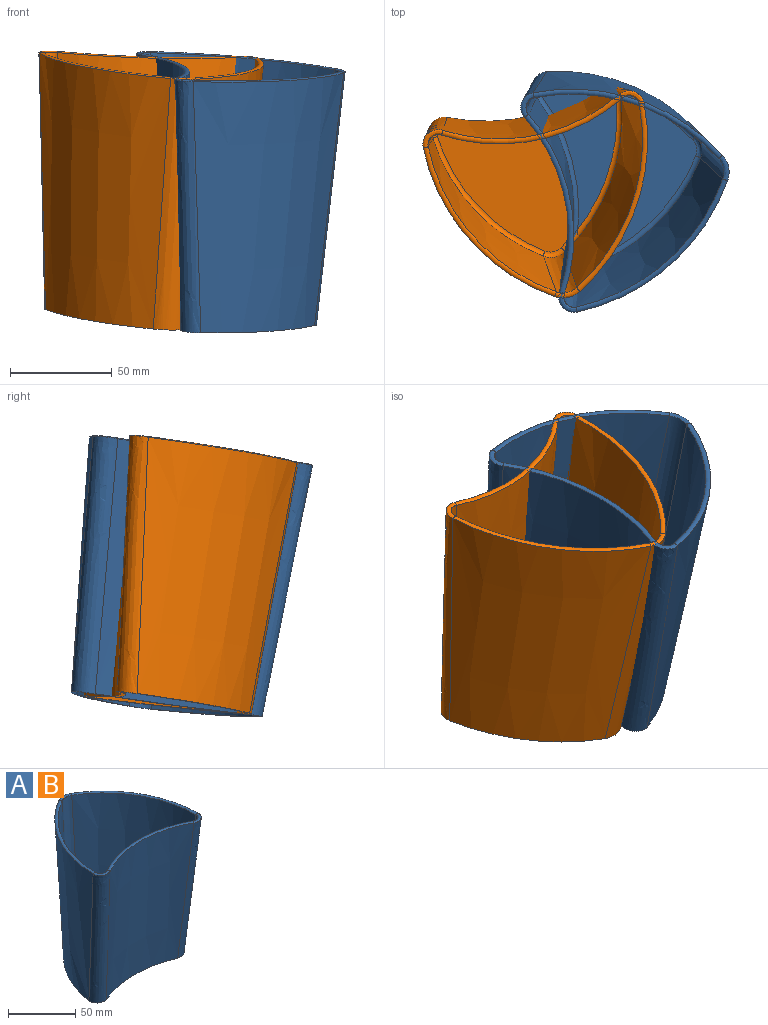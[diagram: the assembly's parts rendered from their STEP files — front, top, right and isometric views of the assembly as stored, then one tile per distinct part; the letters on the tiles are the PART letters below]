
ASSEMBLY  parts=2 mates=1
PART A: 41 faces, bbox 128.3x111x284 mm
  f0: cone r=95mm half-angle=3deg, axis (0,0,-1), area 10624.4mm2, adj f3,f10,f11,f25
  f1: cone r=95mm half-angle=3deg, axis (0,0,1), area 11345.6mm2, adj f3,f10,f13,f23
  f2: cone r=95mm half-angle=3deg, axis (0,0,1), area 11345.6mm2, adj f3,f11,f13,f21
  f3: plane 96.66x76.53mm, normal (0,0,-1), area 542.8mm2, adj f0,f1,f2,f4,f5,f6,f8,f9
  f4: cone r=91.69mm half-angle=3deg, axis (0,0,-1), area 1551.9mm2, adj f3,f8,f12,f18
  f5: cone r=98.31mm half-angle=3deg, axis (0,0,1), area 1591.6mm2, adj f3,f8,f9,f14
  f6: cone r=91.69mm half-angle=3deg, axis (0,0,-1), area 1551.9mm2, adj f3,f9,f12,f17
  f7: plane 84.44x64.14mm, normal (0,0,-1), area 3327.7mm2, adj f14,f15,f16,f17,f18,f19
  f8: bspline ~206.63x27.01mm, area 213mm2, adj f3,f4,f5,f16
  f9: bspline ~155.17x22.59mm, area 213.1mm2, adj f3,f5,f6,f15
  f10: bspline ~212.77x33mm, area 1976.2mm2, adj f0,f1,f3,f24
  f11: bspline ~212.77x33mm, area 1976.2mm2, adj f0,f2,f3,f20
  f12: bspline ~205.45x16.58mm, area 236.5mm2, adj f3,f4,f6,f19
  f13: bspline ~214.01x17.38mm, area 1755.5mm2, adj f1,f2,f3,f22
  f14: torus R=101.86mm, axis (0,0,-1), area 297.4mm2, adj f5,f7,f15,f16
  f15: bspline ~7.89x6.84mm, area 31.6mm2, adj f7,f9,f14,f17
  f16: bspline ~7.89x6.83mm, area 31.6mm2, adj f7,f8,f14,f18
  f17: torus R=88.14mm, axis (0,0,-1), area 282.4mm2, adj f6,f7,f15,f19
  f18: torus R=88.14mm, axis (0,0,-1), area 282.4mm2, adj f4,f7,f16,f19
  f19: bspline ~13.33x4.86mm, area 40.4mm2, adj f7,f12,f17,f18
  f20: bspline ~11.18x7.59mm, area 35.4mm2, adj f11,f21,f25,f40
  f21: torus R=98.99mm, axis (0,0,1), area 273.7mm2, adj f2,f20,f22,f36,f39
  f22: bspline ~12.79x3.91mm, area 32.7mm2, adj f13,f21,f23,f37
  f23: torus R=98.99mm, axis (0,0,1), area 273.7mm2, adj f1,f22,f24,f32,f35
  f24: bspline ~11.18x7.59mm, area 35.4mm2, adj f10,f23,f25,f31
  f25: torus R=91.01mm, axis (0,0,-1), area 252.9mm2, adj f0,f20,f24,f32,f38,f39
  f26: bspline ~8.04x6.63mm, area 31.5mm2, adj f27,f30,f32,f33
  f27: plane 89.6x70.09mm, normal (0,0,1), area 3884.8mm2, adj f26,f28,f29,f30,f33,f34
  f28: bspline ~8.04x6.63mm, area 31.5mm2, adj f27,f30,f34,f39
  f29: bspline ~14.34x4.77mm, area 39.3mm2, adj f27,f33,f34,f37
  f30: torus R=99.74mm, axis (0,0,1), area 318mm2, adj f26,f27,f28,f38
  f31: plane 7.45x5.06mm, normal (0,0,1), area 0.1mm2, adj f24,f32
  f32: bspline ~214x28.45mm, area 1002.6mm2, adj f23,f25,f26,f31,f35,f38
  f33: torus R=90.26mm, axis (0,0,1), area 310mm2, adj f26,f27,f29,f35
  f34: torus R=90.26mm, axis (0,0,1), area 310mm2, adj f27,f28,f29,f36
  f35: cone r=92.5mm half-angle=3deg, axis (0,0,1), area 8676.1mm2, adj f23,f32,f33,f37
  f36: cone r=92.5mm half-angle=3deg, axis (0,0,1), area 8676.1mm2, adj f21,f34,f37,f39
  f37: bspline ~215.75x16.56mm, area 1056.6mm2, adj f22,f29,f35,f36
  f38: cone r=97.5mm half-angle=3deg, axis (0,0,-1), area 8479.3mm2, adj f25,f30,f32,f39
  f39: bspline ~214x28.45mm, area 1001.8mm2, adj f21,f25,f28,f36,f38,f40
  f40: plane 7.97x5.58mm, normal (0,0,1), area 0.1mm2, adj f20,f39
PART B: same geometry as A
PLACE A rot(axis=(0.05,0.09,-0.99),78.9deg) t=(-35.81,-72.83,127.99)mm fixed
PLACE B rot(axis=(-0.02,0.06,-1),168.6deg) t=(-65.92,-64.22,130.63)mm
MATE fastened B.f3 <-> A.f3  axis (0.05,-0.12,0.99) through (-50.31,-110.37,98.85)mm
